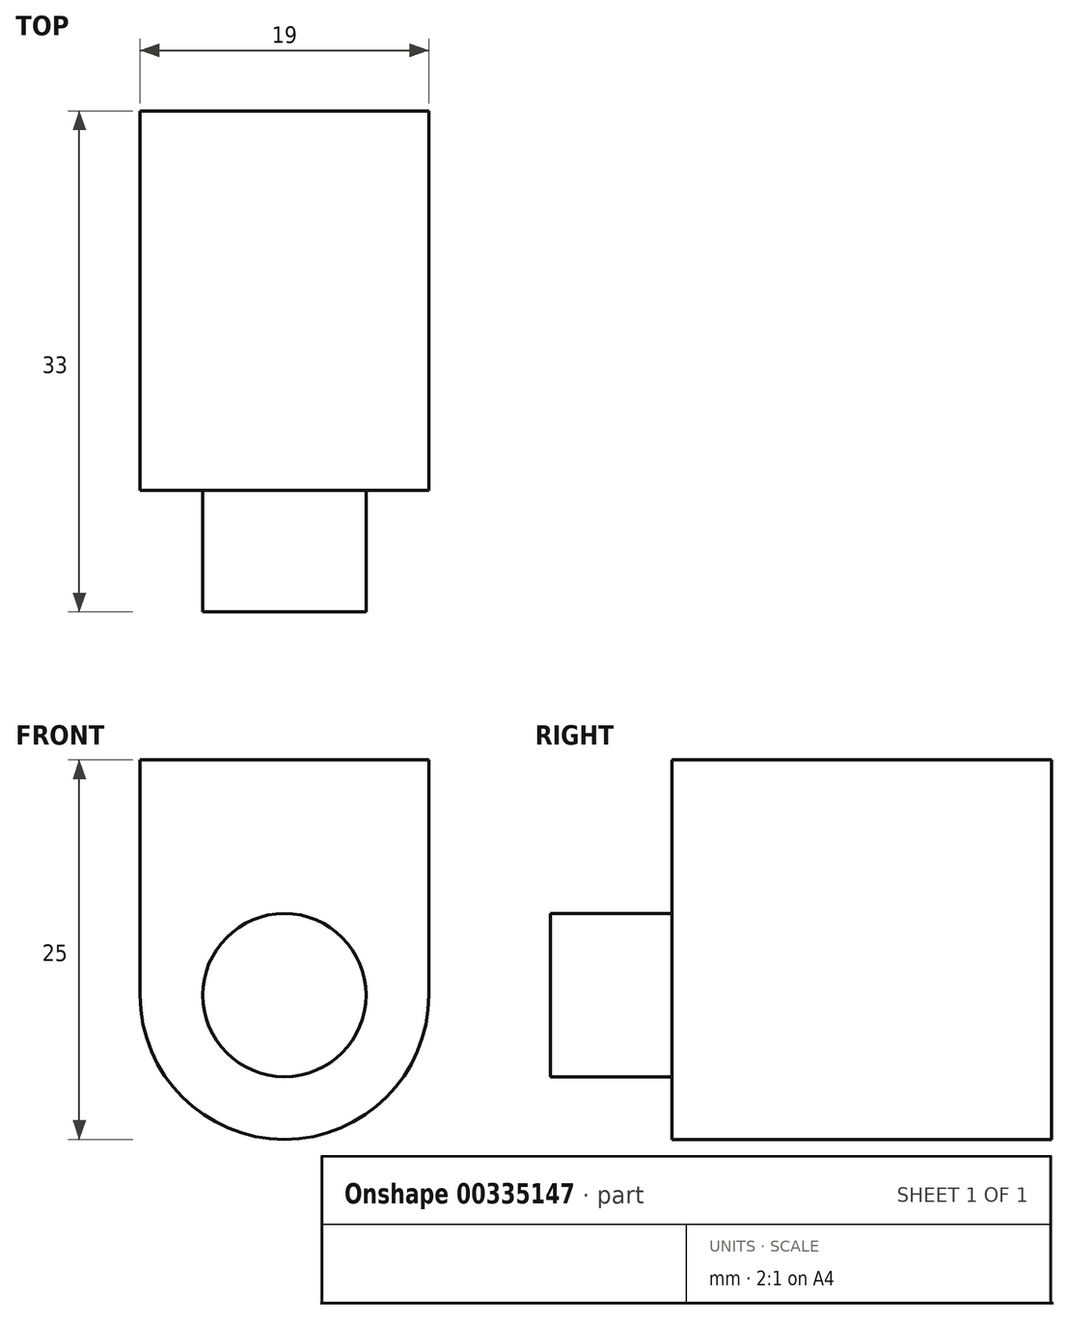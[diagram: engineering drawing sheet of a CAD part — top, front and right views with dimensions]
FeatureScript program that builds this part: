
annotation { "Feature Type Name" : "Feature", "Feature Type Description" : "" }
export const myFeature = defineFeature(function(context is Context, id is Id, definition is map)
    precondition{}
    {
        {
            var Q0;
            Q0=qCreatedBy(makeId("Front.planeOp"),FACE);
            var sketch = newSketch(context, id + "F0", { "sketchPlane" : qUnion([Q0])});
            skArc(sketch, "E0", {"start": v(-9.5, 0) * mm, "mid": v(0, -9.5) * mm, "end": v(9.5, 0) * mm});
            skLineSegment(sketch, "E1", {"start": v(-9.5, 0) * mm, "end": v(-9.5, 15.5) * mm});
            skLineSegment(sketch, "E2", {"start": v(-9.5, 15.5) * mm, "end": v(9.5, 15.5) * mm});
            skLineSegment(sketch, "E3", {"start": v(9.5, 0) * mm, "end": v(9.5, 15.5) * mm});
            skSolve(sketch);
        }
        {
            var Q0;
            Q0 = qSketchRegion(id + "F0", true);
            extrude(context, id + "F1", {"entities" : qUnion([Q0]), "depth" : 25 * mm});
        }
        {
            var Q0;
            Q0=makeQuery(id+"F1.opExtrude","CAP_FACE",FACE,{"disambiguationData":[OSD([sQuery(id+"F0.wireOp",EDGE,"E0"),sQuery(id+"F0.wireOp",EDGE,"E1"),sQuery(id+"F0.wireOp",EDGE,"E2"),sQuery(id+"F0.wireOp",EDGE,"E3")])],"isStart":false});
            var sketch = newSketch(context, id + "F2", { "sketchPlane" : qUnion([Q0])});
            skCircle(sketch, "E4", {"center": v(0, 0) * mm, "radius": 5.38 * mm});
            skSolve(sketch);
        }
        {
            var Q0;
            Q0 = qSketchRegion(id + "F2", true);
            extrude(context, id + "F3", {"entities" : qUnion([Q0]), "operationType" : NewBodyOperationType.ADD, "depth" : 8 * mm});
        }
    });
